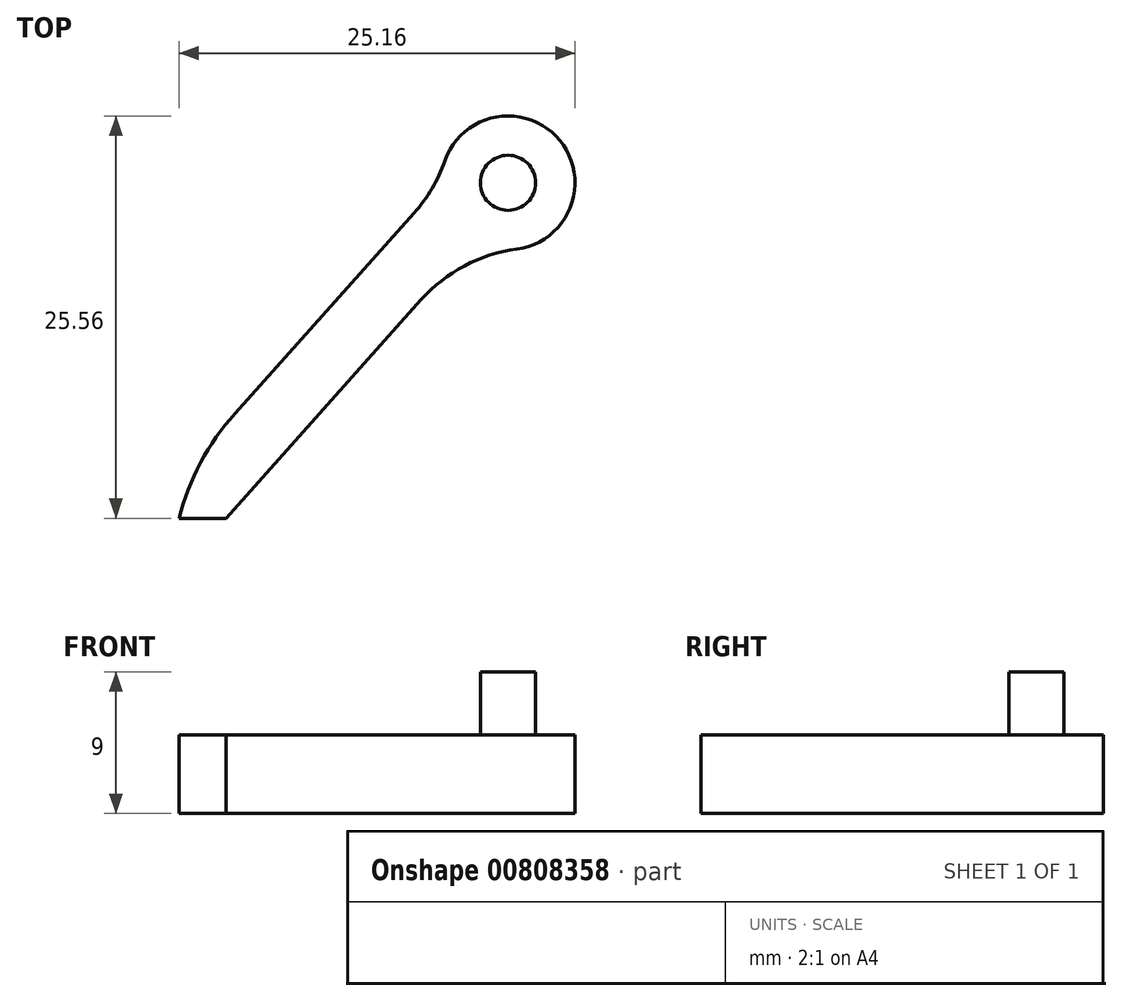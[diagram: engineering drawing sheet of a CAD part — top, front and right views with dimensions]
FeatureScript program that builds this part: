
annotation { "Feature Type Name" : "Feature", "Feature Type Description" : "" }
export const myFeature = defineFeature(function(context is Context, id is Id, definition is map)
    precondition{}
    {
        {
            var Q0;
            Q0=qCreatedBy(makeId("Top.planeOp"),FACE);
            var sketch = newSketch(context, id + "F0", { "sketchPlane" : qUnion([Q0])});
            skCircle(sketch, "E0", {"center": v(12.54, 11.52) * mm, "radius": 4.25 * mm});
            skPoint(sketch, "E0.centerSnap0", {"position": v(9.54, 11.52) * mm});
            skLineSegment(sketch, "E1", {"start": v(8.29, 11.52) * mm, "end": v(-8.37, -7.12) * mm});
            skLineSegment(sketch, "E2", {"start": v(-8.37, -7.12) * mm, "end": v(-5.39, -9.79) * mm});
            skLineSegment(sketch, "E3", {"start": v(-5.39, -9.79) * mm, "end": v(10.38, 7.86) * mm});
            skLineSegment(sketch, "E4", {"start": v(-8.37, -7.12) * mm, "end": v(-8.37, -9.79) * mm});
            skLineSegment(sketch, "E5", {"start": v(-5.39, -9.79) * mm, "end": v(-8.37, -9.79) * mm});
            skCircle(sketch, "E6", {"center": v(12.54, 11.52) * mm, "radius": 1.75 * mm});
            skSolve(sketch);
        }
        {
            var Q0;
            Q0 = qSketchRegion(id + "F0", true);
            extrude(context, id + "F1", {"entities" : qUnion([Q0]), "depth" : 5 * mm, "offsetDistance" : 25 * mm});
        }
        {
            var Q0;
            Q0=makeQuery(id+"F0.imprint","IMPRINT",FACE,{"disambiguationData":[TD([[makeQuery(id+"F0.imprint","IMPRINT",EDGE,{"derivedFrom":sQuery(id+"F0.wireOp",EDGE,"E6")}),1.0]])]});
            extrude(context, id + "F2", {"entities" : qUnion([Q0]), "operationType" : NewBodyOperationType.ADD, "depth" : 9 * mm, "offsetDistance" : 25 * mm});
        }
        {
            var Q0;
            Q0=makeQuery(id+"F1.opExtrude","SWEPT_EDGE",EDGE,{"disambiguationData":[OSD([sQuery(id+"F0.wireOp",EDGE,"E1"),sQuery(id+"F0.wireOp",EDGE,"E2"),sQuery(id+"F0.wireOp",EDGE,"E4")])]});
            fillet(context, id + "F3", {"entities" : qUnion([Q0]), "radius" : 16 * mm, "tangentPropagation" : true, "allowEdgeOverflow" : false});
        }
        {
            var Q0;
            Q0=makeQuery(id+"F1.opExtrude","SWEPT_EDGE",EDGE,{"disambiguationData":[OSD([sQuery(id+"F0.wireOp",EDGE,"E0"),sQuery(id+"F0.wireOp",EDGE,"E1")])]});
            var Q1;
            Q1=makeQuery(id+"F1.opExtrude","SWEPT_EDGE",EDGE,{"disambiguationData":[OSD([sQuery(id+"F0.wireOp",EDGE,"E0"),sQuery(id+"F0.wireOp",EDGE,"E3")])]});
            fillet(context, id + "F4", {"entities" : qUnion([Q0, Q1]), "radius" : 9.88 * mm, "tangentPropagation" : true, "allowEdgeOverflow" : false});
        }
    });
